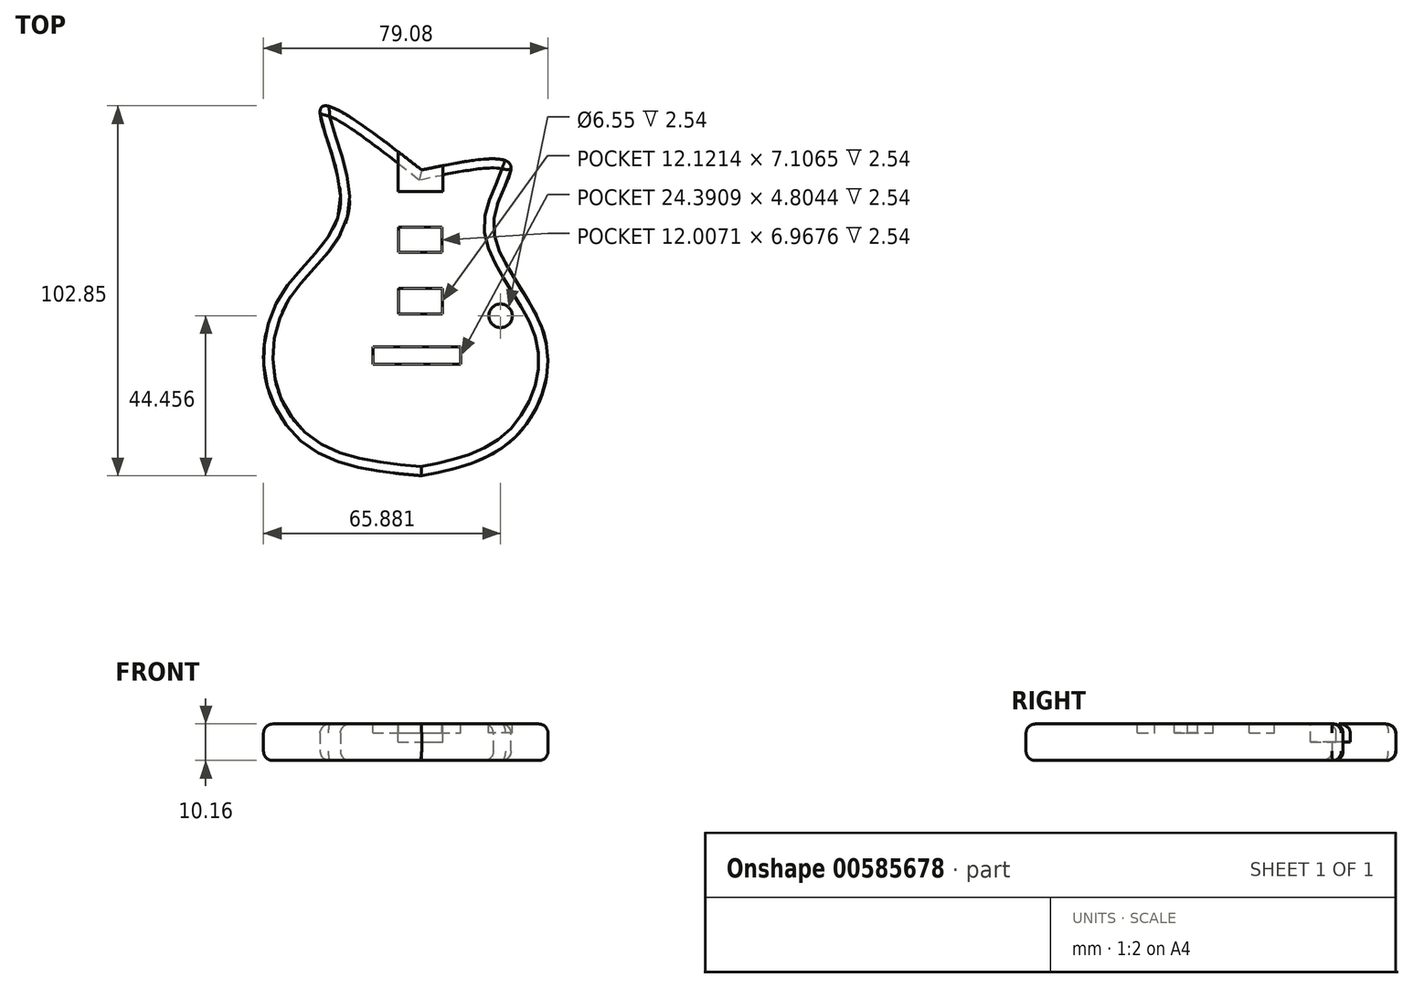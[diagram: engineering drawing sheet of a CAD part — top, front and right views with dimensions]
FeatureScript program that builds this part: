
annotation { "Feature Type Name" : "Feature", "Feature Type Description" : "" }
export const myFeature = defineFeature(function(context is Context, id is Id, definition is map)
    precondition{}
    {
        {
            var Q0;
            Q0=qCreatedBy(makeId("Top.planeOp"),FACE);
            var sketch = newSketch(context, id + "F0", { "sketchPlane" : qUnion([Q0])});
            skFitSpline(sketch, "E0", {"points": [v(0, -52.08) * mm, v(-29.66, -45.23) * mm, v(-43.36, -25.15) * mm, v(-37.92, 0) * mm, v(-22.57, 23.74) * mm, v(-28, 50.19) * mm, v(0, 32.95) * mm], "startDerivative": vector(-186.92, 16.94) * mm, "endDerivative": vector(217.76, -169.37) * mm});
            skFitSpline(sketch, "E1", {"points": [v(0, -52.08) * mm, v(25.14, -42.16) * mm, v(34.35, -13.82) * mm, v(19.94, 17.6) * mm, v(24.67, 34.37) * mm, v(0, 32.95) * mm], "startDerivative": vector(135.38, 27.41) * mm, "endDerivative": vector(-179.77, -37.1) * mm});
            skSolve(sketch);
        }
        {
            var Q0;
            Q0 = qSketchRegion(id + "F0", true);
            extrude(context, id + "F1", {"entities" : qUnion([Q0]), "depth" : 10.16 * mm, "offsetDistance" : 25.4 * mm});
        }
        {
            var Q0;
            Q0=makeQuery(id+"F1.opExtrude","CAP_FACE",FACE,{"disambiguationData":[OSD([sQuery(id+"F0.wireOp",EDGE,"E0"),sQuery(id+"F0.wireOp",EDGE,"E1")])],"isStart":false});
            var sketch = newSketch(context, id + "F2", { "sketchPlane" : qUnion([Q0])});
            skLineSegment(sketch, "E2", {"start": v(-6.58, 38.05) * mm, "end": v(-6.58, 26.94) * mm});
            skLineSegment(sketch, "E3", {"start": v(-6.58, 26.94) * mm, "end": v(5.91, 26.94) * mm});
            skLineSegment(sketch, "E4", {"start": v(5.91, 26.94) * mm, "end": v(5.91, 34.15) * mm});
            skLineSegment(sketch, "E5", {"start": v(5.91, 34.15) * mm, "end": v(0, 32.95) * mm});
            skLineSegment(sketch, "E6", {"start": v(0, 32.95) * mm, "end": v(-6.58, 38.05) * mm});
            skSolve(sketch);
        }
        {
            var Q0;
            Q0=makeQuery(id+"F2.imprint","IMPRINT",FACE,{"disambiguationData":[TD([[makeQuery(id+"F2.imprint","IMPRINT",EDGE,{"derivedFrom":sQuery(id+"F2.wireOp",EDGE,"E2")}),1.0]])]});
            extrude(context, id + "F3", {"entities" : qUnion([Q0]), "operationType" : NewBodyOperationType.REMOVE, "oppositeDirection" : true, "depth" : 5.08 * mm, "offsetDistance" : 25.4 * mm});
        }
        {
            var Q0;
            Q0=makeQuery(id+"F1.opExtrude","CAP_EDGE",EDGE,{"disambiguationData":[OSD([sQuery(id+"F0.wireOp",EDGE,"E1")])],"isStart":true});
            var Q1;
            Q1=makeQuery(id+"F1.opExtrude","CAP_EDGE",EDGE,{"disambiguationData":[OSD([sQuery(id+"F0.wireOp",EDGE,"E1")])],"isStart":false});
            var Q2;
            Q2=makeQuery(id+"F1.opExtrude","CAP_EDGE",EDGE,{"disambiguationData":[OSD([sQuery(id+"F0.wireOp",EDGE,"E0")])],"isStart":true});
            var Q3;
            Q3=makeQuery(id+"F1.opExtrude","CAP_EDGE",EDGE,{"disambiguationData":[OSD([sQuery(id+"F0.wireOp",EDGE,"E0")])],"isStart":false});
            fillet(context, id + "F4", {"entities" : qUnion([Q0, Q1, Q2, Q3]), "radius" : 2.54 * mm, "tangentPropagation" : true, "allowEdgeOverflow" : false});
        }
        {
            var Q0;
            Q0=makeQuery(id+"F1.opExtrude","CAP_FACE",FACE,{"disambiguationData":[OSD([sQuery(id+"F0.wireOp",EDGE,"E0"),sQuery(id+"F0.wireOp",EDGE,"E1")])],"isStart":false});
            var sketch = newSketch(context, id + "F5", { "sketchPlane" : qUnion([Q0])});
            skLineSegment(sketch, "E7.bottom", {"start": v(-6.41, 10.02) * mm, "end": v(5.6, 10.02) * mm});
            skLineSegment(sketch, "E7.top", {"start": v(-6.41, 17) * mm, "end": v(5.6, 17) * mm});
            skLineSegment(sketch, "E7.left", {"start": v(-6.41, 10.02) * mm, "end": v(-6.41, 17) * mm});
            skLineSegment(sketch, "E7.right", {"start": v(5.6, 10.02) * mm, "end": v(5.6, 17) * mm});
            skSolve(sketch);
        }
        {
            var Q0;
            Q0=makeQuery(id+"F5.imprint","IMPRINT",FACE,{"disambiguationData":[TD([[makeQuery(id+"F5.imprint","IMPRINT",EDGE,{"derivedFrom":sQuery(id+"F5.wireOp",EDGE,"E7.bottom")}),-1.0]])]});
            var sketch = newSketch(context, id + "F6", { "sketchPlane" : qUnion([Q0])});
            skLineSegment(sketch, "E8.bottom", {"start": v(-6.37, -7.1) * mm, "end": v(5.75, -7.1) * mm});
            skLineSegment(sketch, "E8.top", {"start": v(-6.37, 0) * mm, "end": v(5.75, 0) * mm});
            skLineSegment(sketch, "E8.left", {"start": v(-6.37, -7.1) * mm, "end": v(-6.37, 0) * mm});
            skLineSegment(sketch, "E8.right", {"start": v(5.75, -7.1) * mm, "end": v(5.75, 0) * mm});
            skLineSegment(sketch, "E9.bottom", {"start": v(-13.56, -21.1) * mm, "end": v(10.83, -21.1) * mm});
            skLineSegment(sketch, "E9.top", {"start": v(-13.56, -16.3) * mm, "end": v(10.83, -16.3) * mm});
            skLineSegment(sketch, "E9.left", {"start": v(-13.56, -21.1) * mm, "end": v(-13.56, -16.3) * mm});
            skLineSegment(sketch, "E9.right", {"start": v(10.83, -21.1) * mm, "end": v(10.83, -16.3) * mm});
            skCircle(sketch, "E10", {"center": v(21.93, -7.62) * mm, "radius": 3.27 * mm});
            skSolve(sketch);
        }
        {
            var Q0;
            Q0=makeQuery(id+"F6.imprint","IMPRINT",FACE,{"disambiguationData":[TD([[makeQuery(id+"F6.imprint","IMPRINT",EDGE,{"derivedFrom":makeQuery(id+"F5.imprint","IMPRINT",EDGE,{"derivedFrom":sQuery(id+"F5.wireOp",EDGE,"E7.bottom")})}),1.0]])]});
            var Q1;
            Q1=makeQuery(id+"F6.imprint","IMPRINT",FACE,{"disambiguationData":[TD([[makeQuery(id+"F6.imprint","IMPRINT",EDGE,{"derivedFrom":sQuery(id+"F6.wireOp",EDGE,"E9.bottom")}),1.0]])]});
            var Q2;
            Q2 = qSketchRegion(id + "F6", true);
            var Q3;
            Q3=makeQuery(id+"F6.imprint","IMPRINT",FACE,{"disambiguationData":[TD([[makeQuery(id+"F6.imprint","IMPRINT",EDGE,{"derivedFrom":sQuery(id+"F6.wireOp",EDGE,"E10")}),1.0]])]});
            var Q4;
            Q4=makeQuery(id+"F6.imprint","IMPRINT",FACE,{"disambiguationData":[TD([[makeQuery(id+"F6.imprint","IMPRINT",EDGE,{"derivedFrom":sQuery(id+"F6.wireOp",EDGE,"E8.bottom")}),1.0]])]});
            extrude(context, id + "F7", {"entities" : qUnion([Q0, Q1, Q2, Q3, Q4]), "operationType" : NewBodyOperationType.REMOVE, "oppositeDirection" : true, "depth" : 2.54 * mm, "offsetDistance" : 25.4 * mm});
        }
    });
